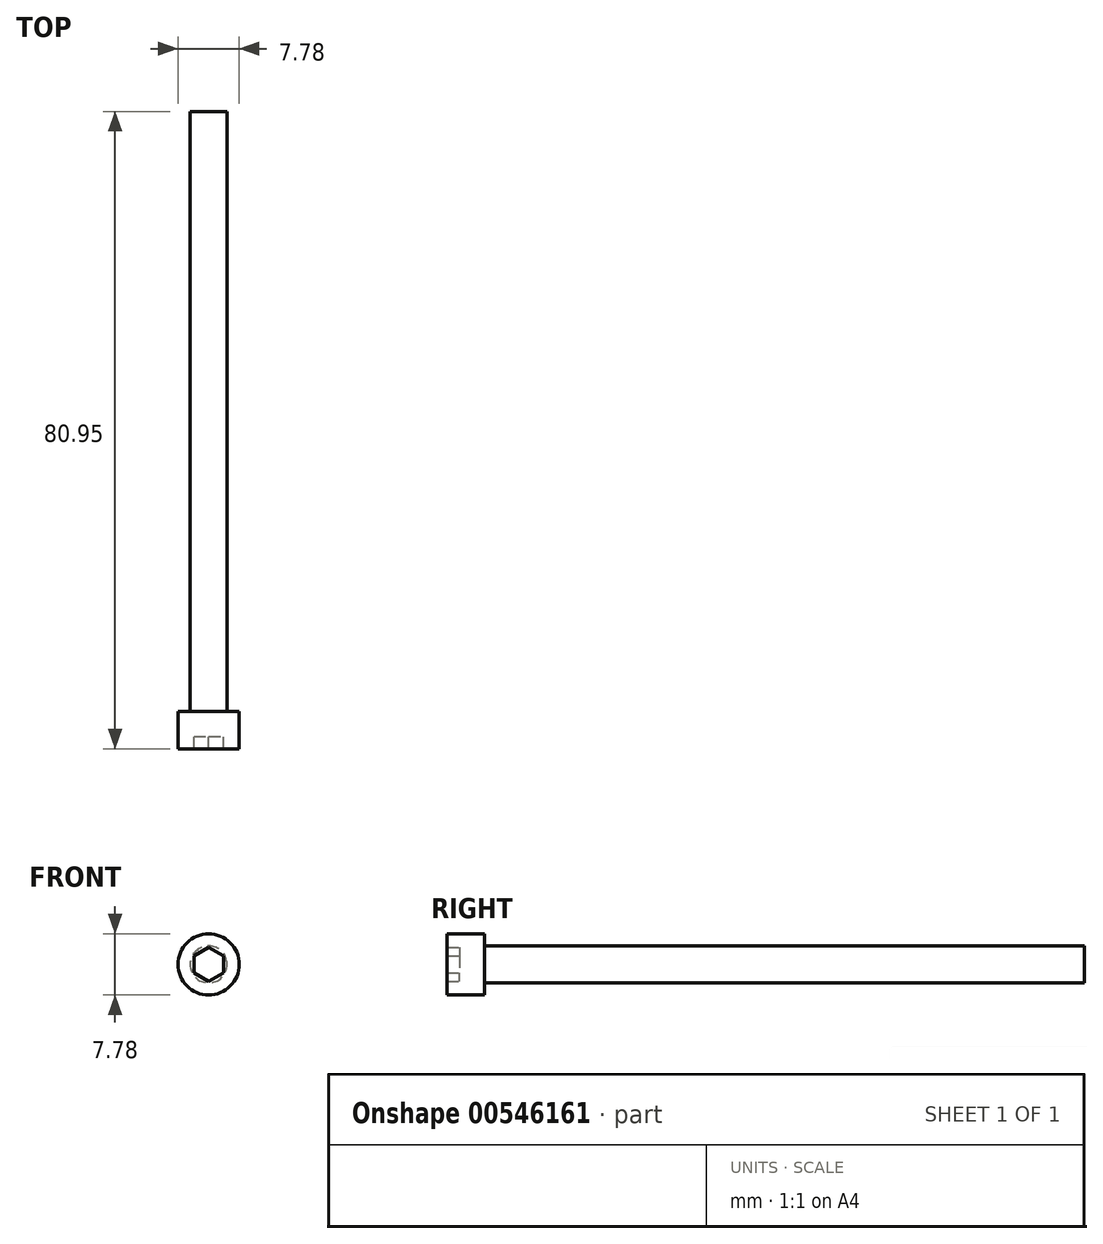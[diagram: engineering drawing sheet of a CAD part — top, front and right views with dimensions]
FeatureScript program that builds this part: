
annotation { "Feature Type Name" : "Feature", "Feature Type Description" : "" }
export const myFeature = defineFeature(function(context is Context, id is Id, definition is map)
    precondition{}
    {
        {
            var Q0;
            Q0=qCreatedBy(makeId("Front.planeOp"),FACE);
            var sketch = newSketch(context, id + "F0", { "sketchPlane" : qUnion([Q0])});
            skCircle(sketch, "E0", {"center": v(0, 0) * mm, "radius": 3.89 * mm});
            skCircle(sketch, "E1.cCircle", {"center": v(0, 0) * mm, "radius": 1.87 * mm, "construction": true});
            skLineSegment(sketch, "E1.0", {"start": v(1.87, 1.08) * mm, "end": v(1.87, -1.08) * mm});
            skLineSegment(sketch, "E1.1", {"start": v(1.87, -1.08) * mm, "end": v(0, -2.16) * mm});
            skLineSegment(sketch, "E1.2", {"start": v(0, -2.16) * mm, "end": v(-1.87, -1.08) * mm});
            skLineSegment(sketch, "E1.3", {"start": v(-1.87, -1.08) * mm, "end": v(-1.87, 1.08) * mm});
            skLineSegment(sketch, "E1.4", {"start": v(-1.87, 1.08) * mm, "end": v(0, 2.16) * mm});
            skLineSegment(sketch, "E1.5", {"start": v(0, 2.16) * mm, "end": v(1.87, 1.08) * mm});
            skPoint(sketch, "E1.0.midPoint", {"position": v(1.87, 0) * mm});
            skSolve(sketch);
        }
        {
            var Q0;
            Q0=makeQuery(id+"F0.imprint","IMPRINT",FACE,{"disambiguationData":[TD([[makeQuery(id+"F0.imprint","IMPRINT",EDGE,{"derivedFrom":sQuery(id+"F0.wireOp",EDGE,"E1.0")}),-1.0]])]});
            extrude(context, id + "F1", {"entities" : qUnion([Q0]), "depth" : 3.17 * mm, "offsetDistance" : 25.4 * mm});
        }
        {
            var Q0;
            Q0 = qSketchRegion(id + "F0", true);
            extrude(context, id + "F2", {"entities" : qUnion([Q0]), "operationType" : NewBodyOperationType.ADD, "depth" : 4.75 * mm, "offsetDistance" : 25.4 * mm});
        }
        {
            var Q0;
            {var subQ0=sQuery(id+"F0.wireOp",EDGE,"E1.5");var subQ1=sQuery(id+"F0.wireOp",EDGE,"E1.4");var subQ2=sQuery(id+"F0.wireOp",EDGE,"E1.3");var subQ3=sQuery(id+"F0.wireOp",EDGE,"E1.2");var subQ4=sQuery(id+"F0.wireOp",EDGE,"E1.1");var subQ5=sQuery(id+"F0.wireOp",EDGE,"E1.0");Q0=makeQuery(id+"F2.boolean.opBoolean","MERGE",FACE,{"derivedFrom":[makeQuery(id+"F1.opExtrude","CAP_FACE",FACE,{"disambiguationData":[OSD([subQ5,subQ4,subQ3,subQ2,subQ1,subQ0])],"isStart":true}),makeQuery(id+"F2.opExtrude","CAP_FACE",FACE,{"disambiguationData":[OSD([sQuery(id+"F0.wireOp",EDGE,"E0"),subQ5,subQ4,subQ3,subQ2,subQ1,subQ0])],"isStart":true})]});}
            var sketch = newSketch(context, id + "F3", { "sketchPlane" : qUnion([Q0])});
            skCircle(sketch, "E2", {"center": v(0, 0) * mm, "radius": 2.35 * mm});
            skSolve(sketch);
        }
        {
            var Q0;
            Q0=makeQuery(id+"F3.imprint","IMPRINT",FACE,{"disambiguationData":[TD([[makeQuery(id+"F3.imprint","IMPRINT",EDGE,{"derivedFrom":sQuery(id+"F3.wireOp",EDGE,"E2")}),1.0]])]});
            extrude(context, id + "F4", {"entities" : qUnion([Q0]), "operationType" : NewBodyOperationType.ADD, "depth" : 76.2 * mm, "offsetDistance" : 25.4 * mm});
        }
    });
